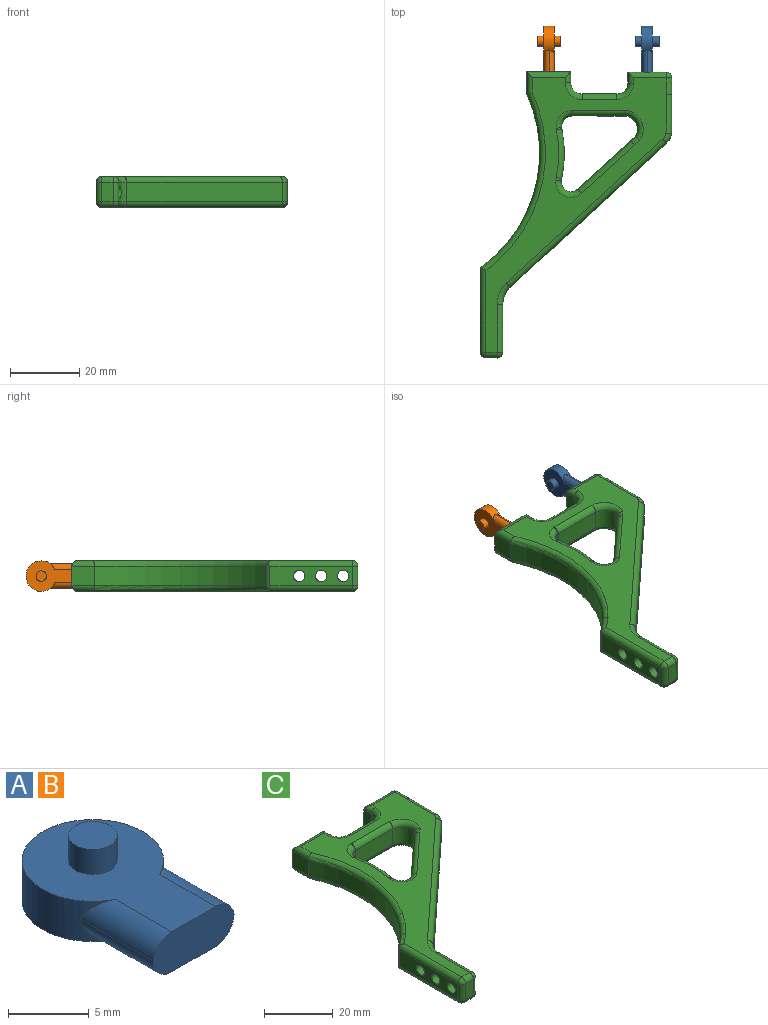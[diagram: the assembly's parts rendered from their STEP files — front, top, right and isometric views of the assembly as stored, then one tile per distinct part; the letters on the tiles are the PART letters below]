
ASSEMBLY  parts=3 mates=2
PART A: 12 faces, bbox 8.8x13.3x6.9 mm
  f0: plane 7.11x3.05mm, normal (0,-1,0), area 19.4mm2, adj f2,f3,f4,f5,f6,f7
  f1: cylinder r=4.4mm len=8.8mm, axis (0,0,-1), area 62.4mm2, adj f2,f3,f4,f5,f6,f7
  f2: plane 13.29x8.8mm, normal (0,0,1), area 71.5mm2, adj f0,f1,f6,f7,f8
  f3: plane 13.29x8.8mm, normal (0,0,-1), area 71.4mm2, adj f0,f1,f4,f5,f10
  f4: cylinder r=1.65mm len=6.24mm, axis (0,1,0), area 14.7mm2, adj f0,f1,f3,f6
  f5: cylinder r=1.65mm len=6.35mm, axis (0,-1,0), area 14.9mm2, adj f0,f1,f3,f7
  f6: cylinder r=1.65mm len=6.24mm, axis (0,1,0), area 13.1mm2, adj f0,f1,f2,f4
  f7: cylinder r=1.65mm len=6.35mm, axis (0,1,0), area 13.3mm2, adj f0,f1,f2,f5
  f8: cylinder r=1.51mm len=3.02mm, axis (0,0,1), area 18.1mm2, adj f2,f9
  f9: plane 3.02x3.02mm, normal (0,0,1), area 7.2mm2, adj f8
  f10: cylinder r=1.5mm len=3mm, axis (0,0,-1), area 18mm2, adj f3,f11
  f11: plane 3x3mm, normal (0,0,-1), area 7.1mm2, adj f10
PART B: same geometry as A
PART C: 105 faces, bbox 55.6x82.7x8.9 mm
  f0: cylinder r=6.01mm len=5.59mm, axis (0,0,-1), area 22.2mm2, adj f17,f18,f58,f61,f104
  f1: plane 5.59x0.32mm, normal (1,0.1,0), area 1.8mm2, adj f2,f31,f87,f97
  f2: cylinder r=3.12mm len=5.59mm, axis (0,0,-1), area 27.4mm2, adj f1,f3,f85,f95
  f3: plane 5.59x0.23mm, normal (0.09,-1,0), area 1.3mm2, adj f2,f4,f83,f93
  f4: plane 15.24x5.59mm, normal (0,-1,0), area 85.1mm2, adj f3,f5,f82,f92
  f5: cylinder r=3.82mm len=5.94mm, axis (0,0,-1), area 44.7mm2, adj f4,f6,f84,f94
  f6: plane 5.59x1.3mm, normal (-0.68,0.73,0), area 9.9mm2, adj f5,f7,f86,f96
  f7: plane 15.31x14.04mm, normal (-0.68,0.74,0), area 116.1mm2, adj f6,f8,f88,f98
  f8: cylinder r=2.79mm len=5.59mm, axis (0,0,-1), area 38.1mm2, adj f7,f9,f90,f100
  f9: plane 5.59x0.67mm, normal (1,-0.08,0), area 3.7mm2, adj f8,f31,f91,f101
  f10: cylinder r=40.59mm len=49.73mm, axis (0,0,-1), area 310.7mm2, adj f11,f30,f35,f36
  f11: cylinder r=1.74mm len=7.07mm, axis (0,0,-1), area 7.7mm2, adj f10,f12,f34,f35,f36,f37
  f12: plane 23.77x5.59mm, normal (-1,0,0), area 107.2mm2, adj f11,f13,f34,f37,f102,f103,f104
  f13: cylinder r=1.65mm len=5.59mm, axis (0,0,-1), area 14.5mm2, adj f12,f14,f38,f41
  f14: plane 5.59x3.26mm, normal (0,-1,0), area 18.2mm2, adj f13,f15,f42,f45
  f15: cylinder r=1.65mm len=5.59mm, axis (0,0,-1), area 14.5mm2, adj f14,f16,f46,f49
  f16: plane 13.64x5.59mm, normal (1,0,0), area 59.1mm2, adj f15,f17,f50,f53,f102,f103
  f17: plane 5.63x0.31mm, normal (1,-0.08,0), area 1.2mm2, adj f0,f16,f54,f57,f104
  f18: plane 5.59x0.13mm, normal (0.77,-0.64,0), area 0.9mm2, adj f0,f19,f62,f65
  f19: plane 44.94x41.6mm, normal (0.68,-0.73,0), area 342.2mm2, adj f18,f20,f66,f70
  f20: cylinder r=4.62mm len=5.59mm, axis (0,0,-1), area 18.2mm2, adj f19,f21,f71,f74
  f21: plane 11.22x5.59mm, normal (1,0,0), area 62.7mm2, adj f20,f75,f78,f81
  f22: plane 5.59x4.83mm, normal (1,0,0), area 27mm2, adj f68,f76,f77,f81
  f23: plane 11.06x5.59mm, normal (0,1,0), area 61.8mm2, adj f24,f67,f68,f69
  f24: plane 5.59x3.15mm, normal (-1,0,0), area 17.6mm2, adj f23,f25,f63,f64
  f25: cylinder r=3.17mm len=5.59mm, axis (0,0,-1), area 27.8mm2, adj f24,f26,f59,f60
  f26: plane 10.05x5.59mm, normal (0,1,0), area 56.2mm2, adj f25,f27,f55,f56
  f27: cylinder r=3.17mm len=5.59mm, axis (0,0,-1), area 28.3mm2, adj f26,f28,f51,f52
  f28: plane 5.59x3.18mm, normal (1,0,0), area 17.8mm2, adj f27,f29,f47,f48
  f29: plane 12.71x5.59mm, normal (0,1,0), area 71mm2, adj f28,f30,f43,f44
  f30: plane 6.46x5.59mm, normal (-1,0,0), area 36.1mm2, adj f10,f29,f39,f40
  f31: cylinder r=34.59mm len=14.37mm, axis (0,0,-1), area 80.9mm2, adj f1,f9,f89,f99
  f32: plane 79.38x51.96mm, normal (0,0,1), area 875.2mm2, adj f34,f35,f39,f42,f43,f47,f50,f51
  f33: plane 79.38x51.96mm, normal (0,0,-1), area 875.2mm2, adj f36,f37,f40,f44,f45,f48,f52,f53
  f34: cylinder r=1.65mm len=24.34mm, axis (0,1,0), area 62.3mm2, adj f11,f12,f32,f35,f38
  f35: torus R=42.24mm, axis (0,0,1), area 146.6mm2, adj f10,f11,f32,f34,f39
  f36: torus R=42.24mm, axis (0,0,1), area 146.6mm2, adj f10,f11,f33,f37,f40
  f37: cylinder r=1.65mm len=24.34mm, axis (0,-1,0), area 62.3mm2, adj f11,f12,f33,f36,f41
  f38: sphere r=1.65mm, area 4.3mm2, adj f13,f34,f42
  f39: cylinder r=1.65mm len=6.46mm, axis (0,1,0), area 14.8mm2, adj f30,f32,f35,f43
  f40: cylinder r=1.65mm len=6.46mm, axis (0,-1,0), area 14.8mm2, adj f30,f33,f36,f44
  f41: sphere r=1.65mm, area 4.3mm2, adj f13,f37,f45
  f42: cylinder r=1.65mm len=3.26mm, axis (-1,0,0), area 8.5mm2, adj f14,f32,f38,f46
  f43: cylinder r=1.65mm len=12.72mm, axis (1,0,0), area 29.9mm2, adj f29,f32,f39,f47
  f44: cylinder r=1.65mm len=12.72mm, axis (-1,0,0), area 29.9mm2, adj f29,f33,f40,f48
  f45: cylinder r=1.65mm len=3.26mm, axis (1,0,0), area 8.5mm2, adj f14,f33,f41,f49
  f46: sphere r=1.65mm, area 4.3mm2, adj f15,f42,f50
  f47: cylinder r=1.65mm len=3.18mm, axis (0,-1,0), area 6.7mm2, adj f28,f32,f43,f51
  f48: cylinder r=1.65mm len=3.18mm, axis (0,1,0), area 6.7mm2, adj f28,f33,f44,f52
  f49: sphere r=1.65mm, area 4.3mm2, adj f15,f45,f53
  f50: cylinder r=1.65mm len=13.7mm, axis (0,-1,0), area 35.5mm2, adj f16,f32,f46,f54
  f51: torus R=4.83mm, axis (0,0,1), area 15.6mm2, adj f27,f32,f47,f55
  f52: torus R=4.83mm, axis (0,0,1), area 15.6mm2, adj f27,f33,f48,f56
  f53: cylinder r=1.65mm len=13.7mm, axis (0,1,0), area 35.5mm2, adj f16,f33,f49,f57
  f54: cylinder r=1.65mm len=1.67mm, axis (-0.08,-1,0), area 0.7mm2, adj f17,f32,f50,f58
  f55: cylinder r=1.65mm len=10.06mm, axis (1,0,0), area 26.1mm2, adj f26,f32,f51,f59
  f56: cylinder r=1.65mm len=10.06mm, axis (-1,0,0), area 26.1mm2, adj f26,f33,f52,f60
  f57: cylinder r=1.65mm len=1.67mm, axis (0.08,1,0), area 0.7mm2, adj f17,f33,f53,f61
  f58: torus R=7.66mm, axis (0,0,1), area 15.4mm2, adj f0,f32,f54,f62
  f59: torus R=4.83mm, axis (0,0,1), area 15.3mm2, adj f25,f32,f55,f63
  f60: torus R=4.83mm, axis (0,0,1), area 15.3mm2, adj f25,f33,f56,f64
  f61: torus R=7.66mm, axis (0,0,1), area 15.4mm2, adj f0,f33,f57,f65
  f62: cylinder r=1.65mm len=1.65mm, axis (-0.64,-0.77,0), area 0.4mm2, adj f18,f32,f58,f66
  f63: cylinder r=1.65mm len=3.15mm, axis (0,1,0), area 6.6mm2, adj f24,f32,f59,f67
  f64: cylinder r=1.65mm len=3.15mm, axis (0,-1,0), area 6.6mm2, adj f24,f33,f60,f69
  f65: cylinder r=1.65mm len=1.65mm, axis (0.64,0.77,0), area 0.4mm2, adj f18,f33,f61,f70
  f66: cylinder r=1.65mm len=46.14mm, axis (-0.73,-0.68,0), area 159mm2, adj f19,f32,f62,f71
  f67: cylinder r=1.65mm len=11.06mm, axis (1,0,0), area 27.1mm2, adj f23,f32,f63,f72
  f68: cylinder r=1.65mm len=5.59mm, axis (0,0,-1), area 14.5mm2, adj f22,f23,f72,f73
  f69: cylinder r=1.65mm len=11.06mm, axis (-1,0,0), area 27.1mm2, adj f23,f33,f64,f73
  f70: cylinder r=1.65mm len=46.14mm, axis (0.73,0.68,0), area 159mm2, adj f19,f33,f65,f74
  f71: torus R=2.97mm, axis (0,0,1), area 7.2mm2, adj f20,f32,f66,f75
  f72: sphere r=1.65mm, area 4.3mm2, adj f67,f68,f76
  f73: sphere r=1.65mm, area 4.3mm2, adj f68,f69,f77
  f74: torus R=2.97mm, axis (0,0,1), area 7.2mm2, adj f20,f33,f70,f78
  f75: cylinder r=1.65mm len=11.23mm, axis (0,-1,0), area 29mm2, adj f21,f32,f71,f79
  f76: cylinder r=1.65mm len=4.83mm, axis (0,-1,0), area 12.5mm2, adj f22,f32,f72,f79
  f77: cylinder r=1.65mm len=4.83mm, axis (0,1,0), area 12.5mm2, adj f22,f33,f73,f80
  f78: cylinder r=1.65mm len=11.23mm, axis (0,1,0), area 29mm2, adj f21,f33,f74,f80
  f79: sphere r=1.65mm, area 0mm2, adj f75,f76,f81
  f80: sphere r=1.65mm, area 0mm2, adj f77,f78,f81
  f81: cylinder r=1.65mm len=5.59mm, axis (0,0,-1), area 0mm2, adj f21,f22,f79,f80
  f82: cylinder r=1.65mm len=15.36mm, axis (1,0,0), area 39.7mm2, adj f4,f33,f83,f84
  f83: cylinder r=1.65mm len=1.67mm, axis (1,0.09,0), area 0.7mm2, adj f3,f33,f82,f85
  f84: torus R=5.47mm, axis (0,0,1), area 24.3mm2, adj f5,f33,f82,f86
  f85: torus R=4.77mm, axis (0,0,1), area 15.2mm2, adj f2,f33,f83,f87
  f86: cylinder r=1.65mm len=2.55mm, axis (-0.73,-0.68,0), area 4.8mm2, adj f6,f33,f84,f88
  f87: cylinder r=1.65mm len=1.68mm, axis (-0.1,1,0), area 1mm2, adj f1,f33,f85,f89
  f88: cylinder r=1.65mm len=16.43mm, axis (-0.74,-0.68,0), area 53.9mm2, adj f7,f33,f86,f90
  f89: torus R=32.94mm, axis (0,0,1), area 37.2mm2, adj f31,f33,f87,f91
  f90: torus R=4.44mm, axis (0,0,1), area 21.4mm2, adj f8,f33,f88,f91
  f91: cylinder r=1.65mm len=1.71mm, axis (0.08,1,0), area 1.8mm2, adj f9,f33,f89,f90
  f92: cylinder r=1.65mm len=15.36mm, axis (-1,0,0), area 39.7mm2, adj f4,f32,f93,f94
  f93: cylinder r=1.65mm len=1.67mm, axis (-1,-0.09,0), area 0.7mm2, adj f3,f32,f92,f95
  f94: torus R=5.47mm, axis (0,0,1), area 24.3mm2, adj f5,f32,f92,f96
  f95: torus R=4.77mm, axis (0,0,1), area 15.2mm2, adj f2,f32,f93,f97
  f96: cylinder r=1.65mm len=2.55mm, axis (0.73,0.68,0), area 4.8mm2, adj f6,f32,f94,f98
  f97: cylinder r=1.65mm len=1.68mm, axis (0.1,-1,0), area 1mm2, adj f1,f32,f95,f99
  f98: cylinder r=1.65mm len=16.43mm, axis (0.74,0.68,0), area 53.9mm2, adj f7,f32,f96,f100
  f99: torus R=32.94mm, axis (0,0,1), area 37.2mm2, adj f31,f32,f97,f101
  f100: torus R=4.44mm, axis (0,0,1), area 21.4mm2, adj f8,f32,f98,f101
  f101: cylinder r=1.65mm len=1.71mm, axis (-0.08,-1,0), area 1.8mm2, adj f9,f32,f99,f100
  f102: cylinder r=1.65mm len=6.57mm, axis (-1,0,0), area 68.1mm2, adj f12,f16
  f103: cylinder r=1.65mm len=6.57mm, axis (-1,0,0), area 68.1mm2, adj f12,f16
  f104: cylinder r=1.65mm len=7.29mm, axis (-1,0,0), area 70.7mm2, adj f0,f12,f17
PLACE A rot(axis=(0,1,0),90deg) t=(11.17,17.79,-9.93)mm
PLACE B rot(axis=(0,1,0),90deg) t=(-17.19,17.84,-9.93)mm
PLACE C rot(axis=(0,0,-1),0.1deg) t=(-22.07,2.35,-2.41)mm
MATE fastened C.f23 <-> A.f0  axis (0,1,0) through (12.71,25.12,2.03)mm
MATE fastened C.f29 <-> B.f0  axis (0,1,0) through (-15.66,25.17,2.03)mm
